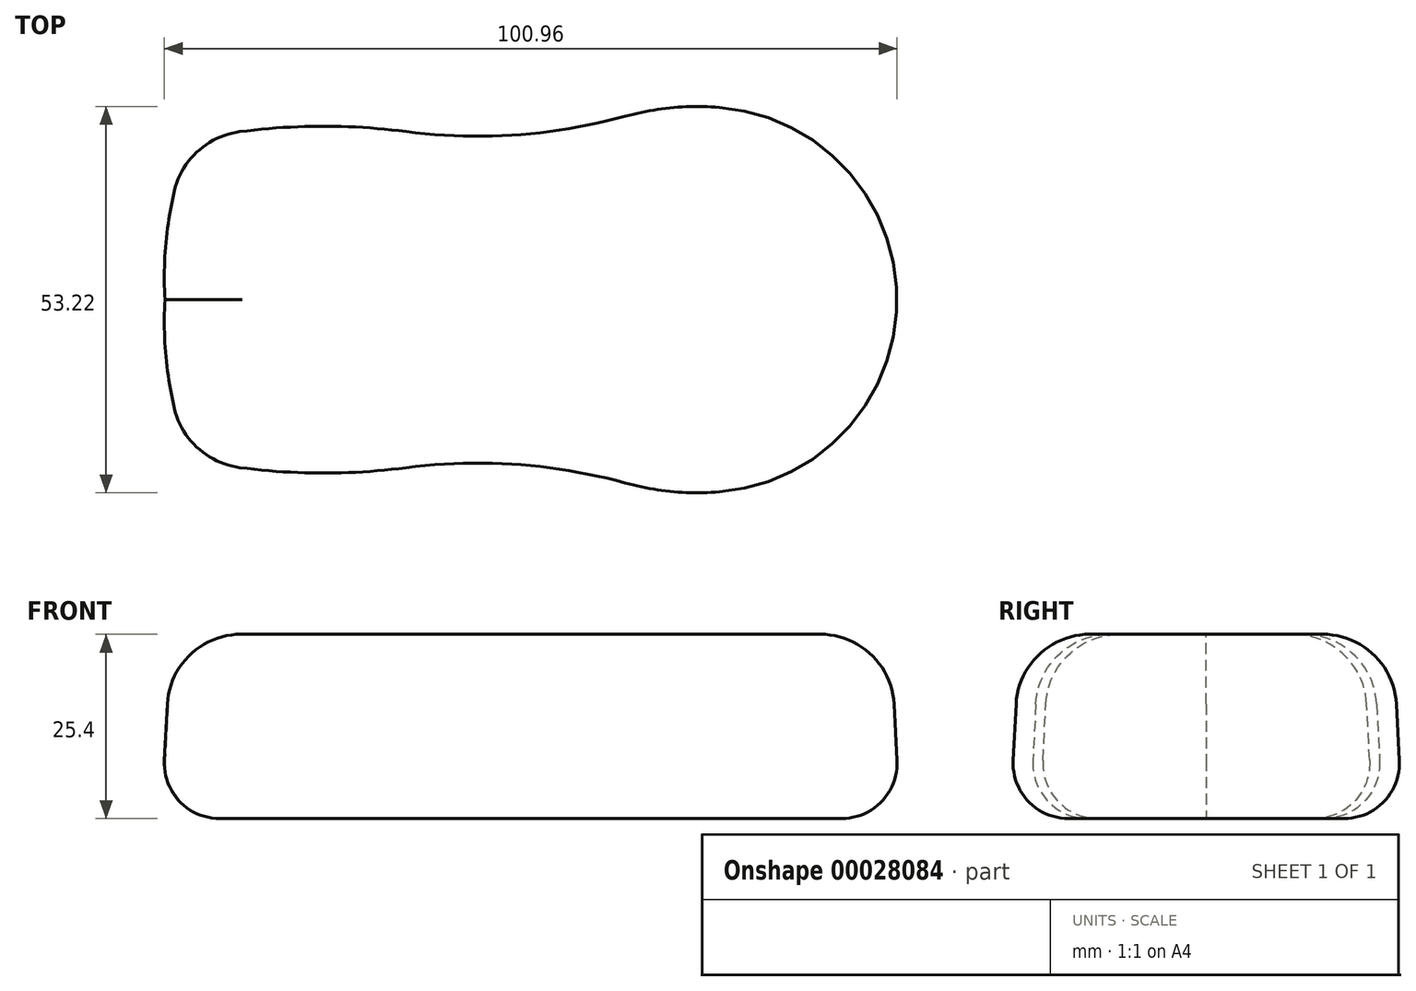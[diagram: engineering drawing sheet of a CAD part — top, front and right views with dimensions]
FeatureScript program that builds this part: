
annotation { "Feature Type Name" : "Feature", "Feature Type Description" : "" }
export const myFeature = defineFeature(function(context is Context, id is Id, definition is map)
    precondition{}
    {
        {
            var Q0;
            Q0=qCreatedBy(makeId("Top.planeOp"),FACE);
            var sketch = newSketch(context, id + "F0", { "sketchPlane" : qUnion([Q0])});
            skArc(sketch, "E0", {"start": v(68.8, 0) * mm, "mid": v(61.65, 18.3) * mm, "end": v(43.99, 26.9) * mm});
            skArc(sketch, "E1", {"start": v(0.79, 23.56) * mm, "mid": v(15.9, 23.11) * mm, "end": v(30.81, 25.66) * mm});
            skLineSegment(sketch, "E2", {"start": v(-58.21, 0) * mm, "end": v(87.68, 0) * mm, "construction": true});
            skArc(sketch, "E3", {"start": v(-22.2, 23.55) * mm, "mid": v(-28.2, 20.79) * mm, "end": v(-31.57, 15.1) * mm});
            skArc(sketch, "E4.trimOffspring", {"start": v(-31.57, 15.1) * mm, "mid": v(-32.79, 7.6) * mm, "end": v(-32.88, 0) * mm});
            skArc(sketch, "E5.trimOffspring", {"start": v(0.79, 23.56) * mm, "mid": v(-10.7, 24.3) * mm, "end": v(-22.2, 23.55) * mm});
            skArc(sketch, "E6.trimOffspring", {"start": v(43.99, 26.9) * mm, "mid": v(37.34, 26.86) * mm, "end": v(30.81, 25.66) * mm});
            skArc(sketch, "E7.MirrorCS", {"start": v(0.79, -23.56) * mm, "mid": v(-10.7, -24.3) * mm, "end": v(-22.2, -23.55) * mm});
            skArc(sketch, "E8.MirrorCS", {"start": v(43.99, -26.9) * mm, "mid": v(37.34, -26.86) * mm, "end": v(30.81, -25.66) * mm});
            skArc(sketch, "E9.MirrorCS", {"start": v(-22.2, -23.55) * mm, "mid": v(-28.2, -20.79) * mm, "end": v(-31.57, -15.1) * mm});
            skArc(sketch, "E10.MirrorCS", {"start": v(0.79, -23.56) * mm, "mid": v(15.9, -23.11) * mm, "end": v(30.81, -25.66) * mm});
            skArc(sketch, "E11.MirrorCS", {"start": v(-31.57, -15.1) * mm, "mid": v(-32.79, -7.6) * mm, "end": v(-32.88, 0) * mm});
            skArc(sketch, "E12.MirrorCS", {"start": v(68.8, 0) * mm, "mid": v(61.65, -18.3) * mm, "end": v(43.99, -26.9) * mm});
            skSolve(sketch);
        }
        {
            var Q0;
            Q0=makeQuery(id+"F0.imprint","IMPRINT",FACE,{"disambiguationData":[TD([[makeQuery(id+"F0.imprint","IMPRINT",EDGE,{"derivedFrom":sQuery(id+"F0.wireOp",EDGE,"E0")}),1.0]])]});
            extrude(context, id + "F1", {"entities" : qUnion([Q0]), "depth" : 25.4 * mm, "hasDraft" : true, "draftAngle" : 3 * degree, "draftPullDirection" : true});
        }
        {
            var Q0;
            Q0=makeQuery(id+"F1.opExtrude","CAP_FACE",FACE,{"disambiguationData":[OSD([sQuery(id+"F0.wireOp",EDGE,"E0"),sQuery(id+"F0.wireOp",EDGE,"E1"),sQuery(id+"F0.wireOp",EDGE,"E3"),sQuery(id+"F0.wireOp",EDGE,"E4.trimOffspring"),sQuery(id+"F0.wireOp",EDGE,"E5.trimOffspring"),sQuery(id+"F0.wireOp",EDGE,"E6.trimOffspring"),sQuery(id+"F0.wireOp",EDGE,"E7.MirrorCS"),sQuery(id+"F0.wireOp",EDGE,"E8.MirrorCS"),sQuery(id+"F0.wireOp",EDGE,"E9.MirrorCS"),sQuery(id+"F0.wireOp",EDGE,"E10.MirrorCS"),sQuery(id+"F0.wireOp",EDGE,"E11.MirrorCS"),sQuery(id+"F0.wireOp",EDGE,"E12.MirrorCS")])],"isStart":false});
            fillet(context, id + "F2", {"entities" : qUnion([Q0]), "radius" : 10.16 * mm, "tangentPropagation" : true, "allowEdgeOverflow" : false});
        }
        {
            var Q0;
            Q0=makeQuery(id+"F1.opExtrude","CAP_FACE",FACE,{"disambiguationData":[OSD([sQuery(id+"F0.wireOp",EDGE,"E0"),sQuery(id+"F0.wireOp",EDGE,"E1"),sQuery(id+"F0.wireOp",EDGE,"E3"),sQuery(id+"F0.wireOp",EDGE,"E4.trimOffspring"),sQuery(id+"F0.wireOp",EDGE,"E5.trimOffspring"),sQuery(id+"F0.wireOp",EDGE,"E6.trimOffspring"),sQuery(id+"F0.wireOp",EDGE,"E7.MirrorCS"),sQuery(id+"F0.wireOp",EDGE,"E8.MirrorCS"),sQuery(id+"F0.wireOp",EDGE,"E9.MirrorCS"),sQuery(id+"F0.wireOp",EDGE,"E10.MirrorCS"),sQuery(id+"F0.wireOp",EDGE,"E11.MirrorCS"),sQuery(id+"F0.wireOp",EDGE,"E12.MirrorCS")])],"isStart":true});
            fillet(context, id + "F3", {"entities" : qUnion([Q0]), "radius" : 7.62 * mm, "tangentPropagation" : true, "allowEdgeOverflow" : false});
        }
    });
